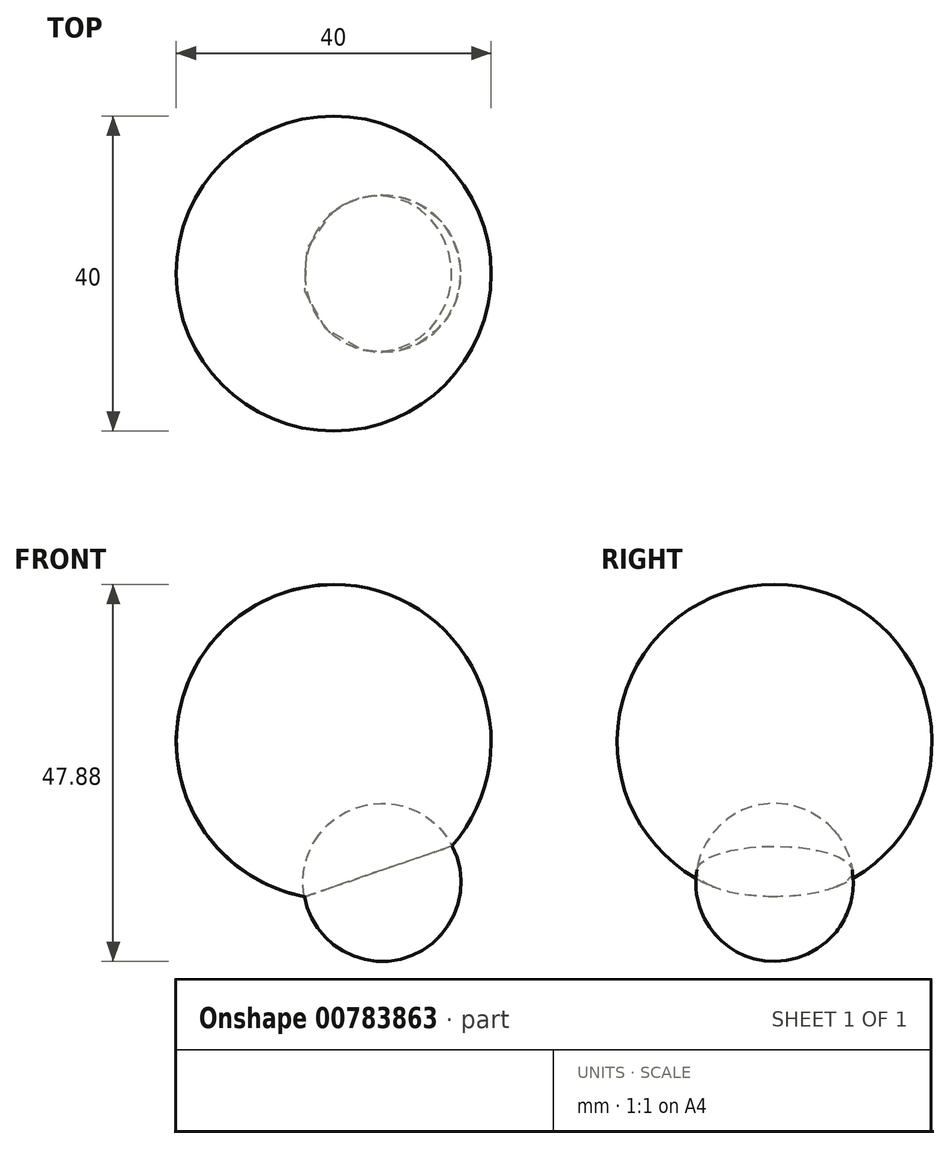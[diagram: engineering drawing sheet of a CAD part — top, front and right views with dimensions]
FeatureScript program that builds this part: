
annotation { "Feature Type Name" : "Feature", "Feature Type Description" : "" }
export const myFeature = defineFeature(function(context is Context, id is Id, definition is map)
    precondition{}
    {
        {
            var Q0;
            Q0=qCreatedBy(makeId("Front.planeOp"),FACE);
            var sketch = newSketch(context, id + "F0", { "sketchPlane" : qUnion([Q0])});
            skLineSegment(sketch, "E0", {"start": v(0, 40) * mm, "end": v(0, 0) * mm});
            skArc(sketch, "E1", {"start": v(0, 0) * mm, "mid": v(20, 20) * mm, "end": v(0, 40) * mm});
            skSolve(sketch);
        }
        {
            var Q0;
            Q0=qCreatedBy(makeId("Front.planeOp"),FACE);
            var sketch = newSketch(context, id + "F1", { "sketchPlane" : qUnion([Q0])});
            skLineSegment(sketch, "E2", {"start": v(0, 39.93) * mm, "end": v(0, 0) * mm, "construction": true});
            skLineSegment(sketch, "E3", {"start": v(0, 19.96) * mm, "end": v(18.89, 26.47) * mm, "construction": true});
            skSolve(sketch);
        }
        {
            var Q0;
            Q0=sQuery(id+"F0.wireOp",VERTEX,"E1.center");
            var Q1;
            Q1=sQuery(id+"F1.wireOp",EDGE,"E3");
            cPlane(context, id + "F2", {"entities" : qUnion([Q0, Q1]), "cplaneType" : CPlaneType.LINE_POINT, "offset" : 25 * mm, "width" : 150 * mm, "height" : 150 * mm});
        }
        {
            var Q0;
            Q0 = qSketchRegion(id + "F0", true);
            var Q1;
            Q1=sQuery(id+"F0.wireOp",EDGE,"E0");
            revolve(context, id + "F3", {"surfaceOperationType" : NewSurfaceOperationType.NEW, "entities" : qUnion([Q0]), "axis" : qUnion([Q1]), "revolveType" : RevolveType.FULL});
        }
        {
            var Q0;
            Q0=qCreatedBy(id+"F2.planeOp",FACE);
            var sketch = newSketch(context, id + "F4", { "sketchPlane" : qUnion([Q0])});
            skLineSegment(sketch, "E4", {"start": v(10, 0.04) * mm, "end": v(-10, 0.04) * mm});
            skArc(sketch, "E5", {"start": v(10, 0.04) * mm, "mid": v(0, 10) * mm, "end": v(-10, 0.04) * mm});
            skSolve(sketch);
        }
        {
            var Q0;
            Q0 = qSketchRegion(id + "F4", true);
            var Q1;
            Q1=sQuery(id+"F4.wireOp",EDGE,"E4");
            revolve(context, id + "F5", {"operationType" : NewBodyOperationType.ADD, "surfaceOperationType" : NewSurfaceOperationType.NEW, "entities" : qUnion([Q0]), "axis" : qUnion([Q1]), "revolveType" : RevolveType.FULL});
        }
    });
